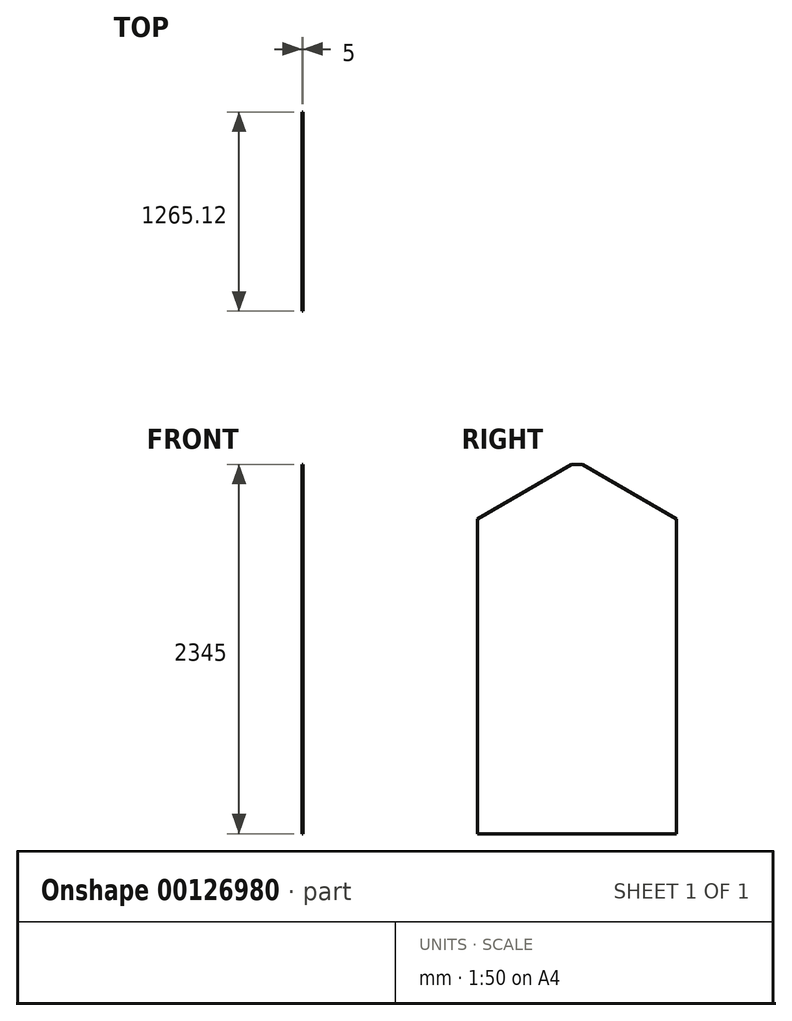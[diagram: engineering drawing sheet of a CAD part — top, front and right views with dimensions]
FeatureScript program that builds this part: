
annotation { "Feature Type Name" : "Feature", "Feature Type Description" : "" }
export const myFeature = defineFeature(function(context is Context, id is Id, definition is map)
    precondition{}
    {
        {
            var Q0;
            Q0=qCreatedBy(makeId("Right.planeOp"),FACE);
            var sketch = newSketch(context, id + "F0", { "sketchPlane" : qUnion([Q0])});
            skLineSegment(sketch, "E0", {"start": v(0, 0) * mm, "end": v(-35, 0) * mm});
            skLineSegment(sketch, "E1", {"start": v(-35, 0) * mm, "end": v(-632.56, -345) * mm});
            skLineSegment(sketch, "E2", {"start": v(-632.56, -345) * mm, "end": v(-632.56, -2345) * mm});
            skLineSegment(sketch, "E3.MirrorCS", {"start": v(35, 0) * mm, "end": v(632.56, -345) * mm});
            skLineSegment(sketch, "E4.MirrorCS", {"start": v(632.56, -345) * mm, "end": v(632.56, -2345) * mm});
            skLineSegment(sketch, "E5.MirrorCS", {"start": v(0, 0) * mm, "end": v(35, 0) * mm});
            skPoint(sketch, "E6.end.orphan", {"position": v(0, -1945) * mm});
            skLineSegment(sketch, "E7", {"start": v(632.56, -2345) * mm, "end": v(-632.56, -2345) * mm});
            skSolve(sketch);
        }
        {
            var Q0;
            Q0 = qSketchRegion(id + "F0", true);
            extrude(context, id + "F1", {"entities" : qUnion([Q0]), "depth" : 5 * mm});
        }
    });
